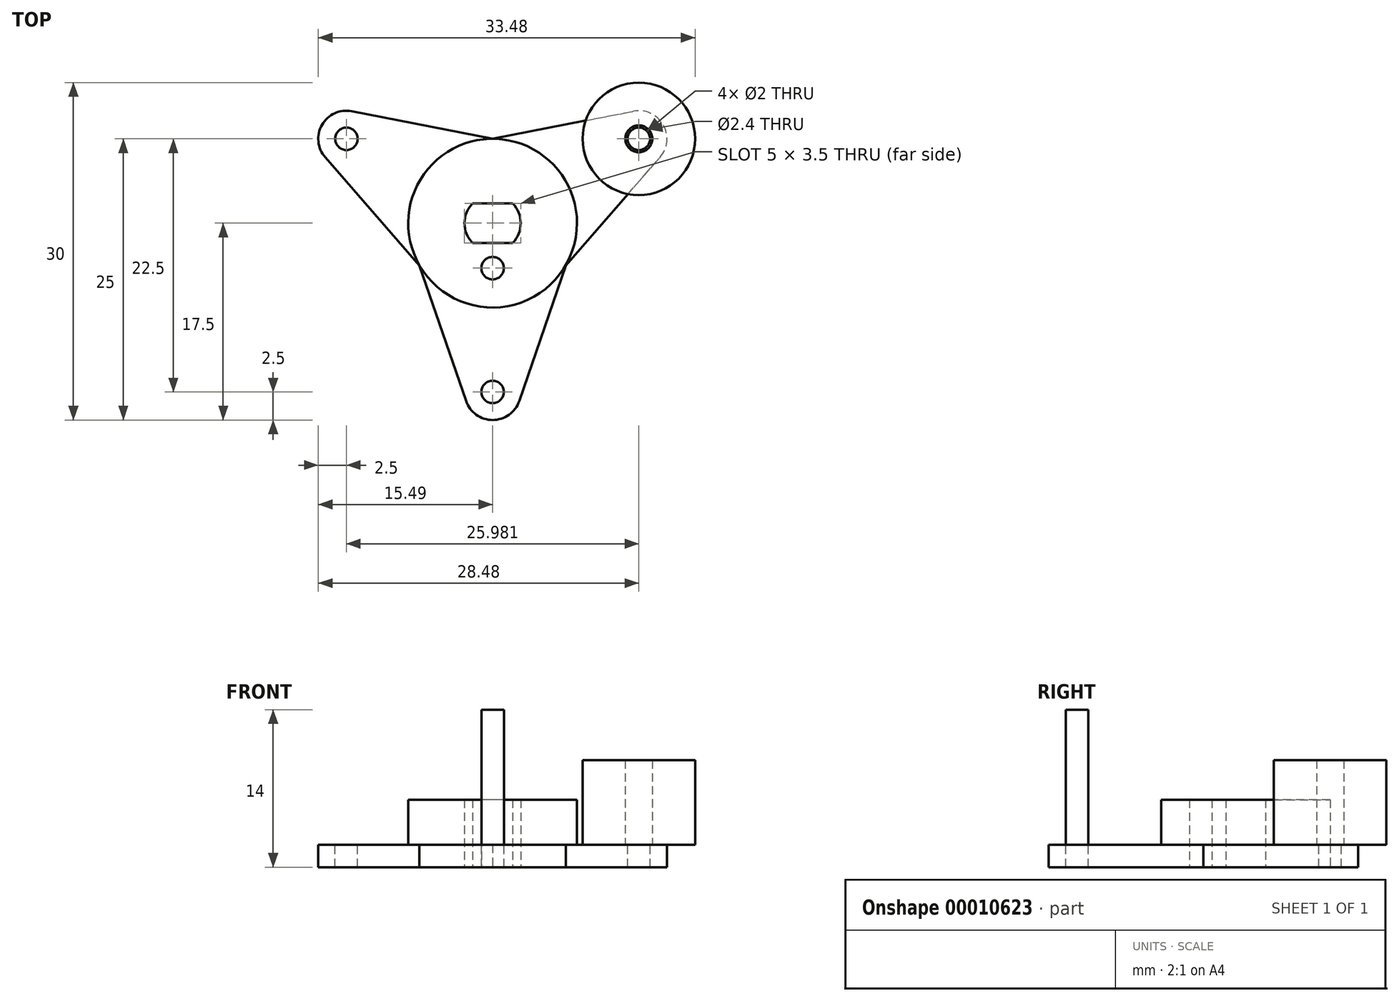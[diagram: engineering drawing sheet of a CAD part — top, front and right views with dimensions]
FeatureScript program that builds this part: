
annotation { "Feature Type Name" : "Feature", "Feature Type Description" : "" }
export const myFeature = defineFeature(function(context is Context, id is Id, definition is map)
    precondition{}
    {
        {
            var Q0;
            Q0=qCreatedBy(makeId("Top.planeOp"),FACE);
            var sketch = newSketch(context, id + "F0", { "sketchPlane" : qUnion([Q0])});
            skCircle(sketch, "E0.cCircle", {"center": v(0, 0) * mm, "radius": 7.5 * mm, "construction": true});
            skLineSegment(sketch, "E0.0", {"start": v(-13, 7.5) * mm, "end": v(13, 7.5) * mm});
            skLineSegment(sketch, "E0.1", {"start": v(13, 7.5) * mm, "end": v(0, -15) * mm});
            skLineSegment(sketch, "E0.2", {"start": v(0, -15) * mm, "end": v(-13, 7.5) * mm});
            skPoint(sketch, "E0.0.midPoint", {"position": v(0, 7.5) * mm});
            skCircle(sketch, "E1", {"center": v(-13, 7.5) * mm, "radius": 5 * mm, "construction": true});
            skCircle(sketch, "E2", {"center": v(13, 7.5) * mm, "radius": 5 * mm, "construction": true});
            skCircle(sketch, "E3", {"center": v(0, -15) * mm, "radius": 5 * mm, "construction": true});
            skCircle(sketch, "E4", {"center": v(0, 0) * mm, "radius": 20 * mm, "construction": true});
            skArc(sketch, "E5", {"start": v(-10.5, 7.5) * mm, "mid": v(-15.16, 8.75) * mm, "end": v(-11.74, 5.33) * mm});
            skArc(sketch, "E6", {"start": v(11.74, 5.33) * mm, "mid": v(15.16, 8.75) * mm, "end": v(10.5, 7.5) * mm});
            skArc(sketch, "E7", {"start": v(-1.25, -12.83) * mm, "mid": v(0, -17.5) * mm, "end": v(1.25, -12.83) * mm});
            skLineSegment(sketch, "E8", {"start": v(-6.5, -3.75) * mm, "end": v(-14.87, 5.86) * mm});
            skLineSegment(sketch, "E9", {"start": v(0, 7.5) * mm, "end": v(-12.5, 9.95) * mm});
            skLineSegment(sketch, "E10.1.0", {"start": v(-6.5, -3.75) * mm, "end": v(-2.37, -15.8) * mm});
            skLineSegment(sketch, "E10.1.1", {"start": v(6.5, -3.75) * mm, "end": v(2.37, -15.8) * mm});
            skLineSegment(sketch, "E10.2.0", {"start": v(6.5, -3.75) * mm, "end": v(14.87, 5.86) * mm});
            skLineSegment(sketch, "E10.2.1", {"start": v(0, 7.5) * mm, "end": v(12.5, 9.95) * mm});
            skSolve(sketch);
        }
        {
            var Q0;
            Q0=qSketchRegion(id+"F0",true);
            extrude(context, id + "F1", {"entities" : qUnion([Q0]), "depth" : 2 * mm});
        }
        {
            var Q0;
            Q0=makeQuery(id+"F1.opExtrude","CAP_FACE",FACE,{"disambiguationData":[OSD([sQuery(id+"F0.wireOp",EDGE,"E5"),sQuery(id+"F0.wireOp",EDGE,"E6"),sQuery(id+"F0.wireOp",EDGE,"E7"),sQuery(id+"F0.wireOp",EDGE,"E8"),sQuery(id+"F0.wireOp",EDGE,"E9"),sQuery(id+"F0.wireOp",EDGE,"E10.1.0"),sQuery(id+"F0.wireOp",EDGE,"E10.1.1"),sQuery(id+"F0.wireOp",EDGE,"E10.2.0"),sQuery(id+"F0.wireOp",EDGE,"E10.2.1")])],"isStart":true});
            var sketch = newSketch(context, id + "F2", { "sketchPlane" : qUnion([Q0])});
            skArc(sketch, "E11", {"start": v(-1.79, 1.75) * mm, "mid": v(-2.5, 0) * mm, "end": v(-1.79, -1.75) * mm});
            skLineSegment(sketch, "E12.rect.bottom", {"start": v(-1.79, 1.75) * mm, "end": v(1.79, 1.75) * mm});
            skLineSegment(sketch, "E12.rect.top", {"start": v(-1.79, -1.75) * mm, "end": v(1.79, -1.75) * mm});
            skLineSegment(sketch, "E12.rect.left", {"start": v(-1.79, 1.75) * mm, "end": v(-1.79, -1.75) * mm});
            skLineSegment(sketch, "E12.rect.right", {"start": v(1.79, 1.75) * mm, "end": v(1.79, -1.75) * mm});
            skArc(sketch, "E13.trimOffspring", {"start": v(1.79, -1.75) * mm, "mid": v(2.5, 0) * mm, "end": v(1.79, 1.75) * mm});
            skCircle(sketch, "E14", {"center": v(0, 4) * mm, "radius": 1 * mm});
            skPoint(sketch, "E14.centerSnap0", {"position": v(0, 1.75) * mm});
            skSolve(sketch);
        }
        {
            var Q0;
            Q0=qSketchRegion(id+"F2",true);
            extrude(context, id + "F3", {"entities" : qUnion([Q0]), "operationType" : NewBodyOperationType.REMOVE, "endBound" : BoundingType.THROUGH_ALL, "oppositeDirection" : true, "depth" : 25 * mm});
        }
        {
            var Q0;
            Q0=makeQuery(id+"F1.opExtrude","CAP_FACE",FACE,{"disambiguationData":[OSD([sQuery(id+"F0.wireOp",EDGE,"E5"),sQuery(id+"F0.wireOp",EDGE,"E6"),sQuery(id+"F0.wireOp",EDGE,"E7"),sQuery(id+"F0.wireOp",EDGE,"E8"),sQuery(id+"F0.wireOp",EDGE,"E9"),sQuery(id+"F0.wireOp",EDGE,"E10.1.0"),sQuery(id+"F0.wireOp",EDGE,"E10.1.1"),sQuery(id+"F0.wireOp",EDGE,"E10.2.0"),sQuery(id+"F0.wireOp",EDGE,"E10.2.1")])],"isStart":false});
            var sketch = newSketch(context, id + "F4", { "sketchPlane" : qUnion([Q0])});
            skCircle(sketch, "E15", {"center": v(0, 0) * mm, "radius": 7.5 * mm});
            skLineSegment(sketch, "E16.0", {"start": v(1.79, 1.75) * mm, "end": v(-1.79, 1.75) * mm});
            skArc(sketch, "E16.1", {"start": v(-1.79, 1.75) * mm, "mid": v(-2.5, 0) * mm, "end": v(-1.79, -1.75) * mm});
            skLineSegment(sketch, "E16.2", {"start": v(1.79, -1.75) * mm, "end": v(-1.79, -1.75) * mm});
            skArc(sketch, "E16.3", {"start": v(1.79, -1.75) * mm, "mid": v(2.5, 0) * mm, "end": v(1.79, 1.75) * mm});
            skCircle(sketch, "E17.0", {"center": v(0, -4) * mm, "radius": 1 * mm});
            skSolve(sketch);
        }
        {
            var Q0;
            Q0=qSketchRegion(id+"F4",true);
            extrude(context, id + "F5", {"entities" : qUnion([Q0]), "operationType" : NewBodyOperationType.ADD, "depth" : 4 * mm});
        }
        {
            var Q0;
            {var subQ0=sQuery(id+"F0.wireOp",EDGE,"E5");var subQ1=sQuery(id+"F0.wireOp",EDGE,"E8");var subQ2=sQuery(id+"F0.wireOp",EDGE,"E9");var subQ3=sQuery(id+"F0.wireOp",EDGE,"E10.1.0");var subQ4=sQuery(id+"F0.wireOp",EDGE,"E10.2.1");var subQ5=makeQuery(id+"F1.opExtrude","CAP_FACE",FACE,{"disambiguationData":[OSD([subQ0,sQuery(id+"F0.wireOp",EDGE,"E6"),sQuery(id+"F0.wireOp",EDGE,"E7"),subQ1,subQ2,subQ3,sQuery(id+"F0.wireOp",EDGE,"E10.1.1"),sQuery(id+"F0.wireOp",EDGE,"E10.2.0"),subQ4])],"isStart":false});Q0=makeQuery(id+"F5.boolean.opBoolean","SPLIT",FACE,{"disambiguationData":[TD([makeQuery(id+"F1.opExtrude","SWEPT_FACE",FACE,{"disambiguationData":[OSD([subQ0])]})])],"derivedFrom":subQ5});}
            var sketch = newSketch(context, id + "F6", { "sketchPlane" : qUnion([Q0])});
            skCircle(sketch, "E18", {"center": v(-13, 7.5) * mm, "radius": 1 * mm});
            skCircle(sketch, "E19.1.0", {"center": v(0, -15) * mm, "radius": 1 * mm});
            skCircle(sketch, "E19.2.0", {"center": v(13, 7.5) * mm, "radius": 1 * mm});
            skPoint(sketch, "E19.center", {"position": v(0, 0) * mm});
            skSolve(sketch);
        }
        {
            var Q0;
            Q0=qSketchRegion(id+"F6",true);
            extrude(context, id + "F7", {"entities" : qUnion([Q0]), "operationType" : NewBodyOperationType.REMOVE, "endBound" : BoundingType.THROUGH_ALL, "oppositeDirection" : true, "depth" : 25 * mm});
        }
        {
            var Q0;
            {var subQ0=sQuery(id+"F0.wireOp",EDGE,"E7");var subQ1=sQuery(id+"F0.wireOp",EDGE,"E8");var subQ2=sQuery(id+"F0.wireOp",EDGE,"E10.1.0");var subQ3=sQuery(id+"F0.wireOp",EDGE,"E10.1.1");var subQ4=sQuery(id+"F0.wireOp",EDGE,"E10.2.0");var subQ5=makeQuery(id+"F1.opExtrude","CAP_FACE",FACE,{"disambiguationData":[OSD([sQuery(id+"F0.wireOp",EDGE,"E5"),sQuery(id+"F0.wireOp",EDGE,"E6"),subQ0,subQ1,sQuery(id+"F0.wireOp",EDGE,"E9"),subQ2,subQ3,subQ4,sQuery(id+"F0.wireOp",EDGE,"E10.2.1")])],"isStart":false});Q0=makeQuery(id+"F5.boolean.opBoolean","SPLIT",FACE,{"disambiguationData":[TD([makeQuery(id+"F1.opExtrude","SWEPT_FACE",FACE,{"disambiguationData":[OSD([subQ0])]})])],"derivedFrom":subQ5});}
            var sketch = newSketch(context, id + "F8", { "sketchPlane" : qUnion([Q0])});
            skCircle(sketch, "E20.0", {"center": v(0, -15) * mm, "radius": 1 * mm});
            skSolve(sketch);
        }
        {
            var Q0;
            Q0=qSketchRegion(id+"F8",true);
            extrude(context, id + "F9", {"entities" : qUnion([Q0]), "depth" : 12 * mm});
        }
        {
            var Q0;
            {var subQ0=sQuery(id+"F0.wireOp",EDGE,"E6");var subQ1=sQuery(id+"F0.wireOp",EDGE,"E9");var subQ2=sQuery(id+"F0.wireOp",EDGE,"E10.1.1");var subQ3=sQuery(id+"F0.wireOp",EDGE,"E10.2.0");var subQ4=sQuery(id+"F0.wireOp",EDGE,"E10.2.1");var subQ5=makeQuery(id+"F1.opExtrude","CAP_FACE",FACE,{"disambiguationData":[OSD([sQuery(id+"F0.wireOp",EDGE,"E5"),subQ0,sQuery(id+"F0.wireOp",EDGE,"E7"),sQuery(id+"F0.wireOp",EDGE,"E8"),subQ1,sQuery(id+"F0.wireOp",EDGE,"E10.1.0"),subQ2,subQ3,subQ4])],"isStart":false});Q0=makeQuery(id+"F5.boolean.opBoolean","SPLIT",FACE,{"disambiguationData":[TD([makeQuery(id+"F1.opExtrude","SWEPT_FACE",FACE,{"disambiguationData":[OSD([subQ0])]})])],"derivedFrom":subQ5});}
            var sketch = newSketch(context, id + "F10", { "sketchPlane" : qUnion([Q0])});
            skCircle(sketch, "E21.0", {"center": v(13, 7.5) * mm, "radius": 1 * mm, "construction": true});
            skCircle(sketch, "E22", {"center": v(13, 7.5) * mm, "radius": 5 * mm});
            skCircle(sketch, "E23.0", {"center": v(13, 7.5) * mm, "radius": 1.2 * mm});
            skSolve(sketch);
        }
        {
            var Q0;
            Q0=qSketchRegion(id+"F10",true);
            extrude(context, id + "F11", {"entities" : qUnion([Q0]), "depth" : 7.5 * mm});
        }
    });
